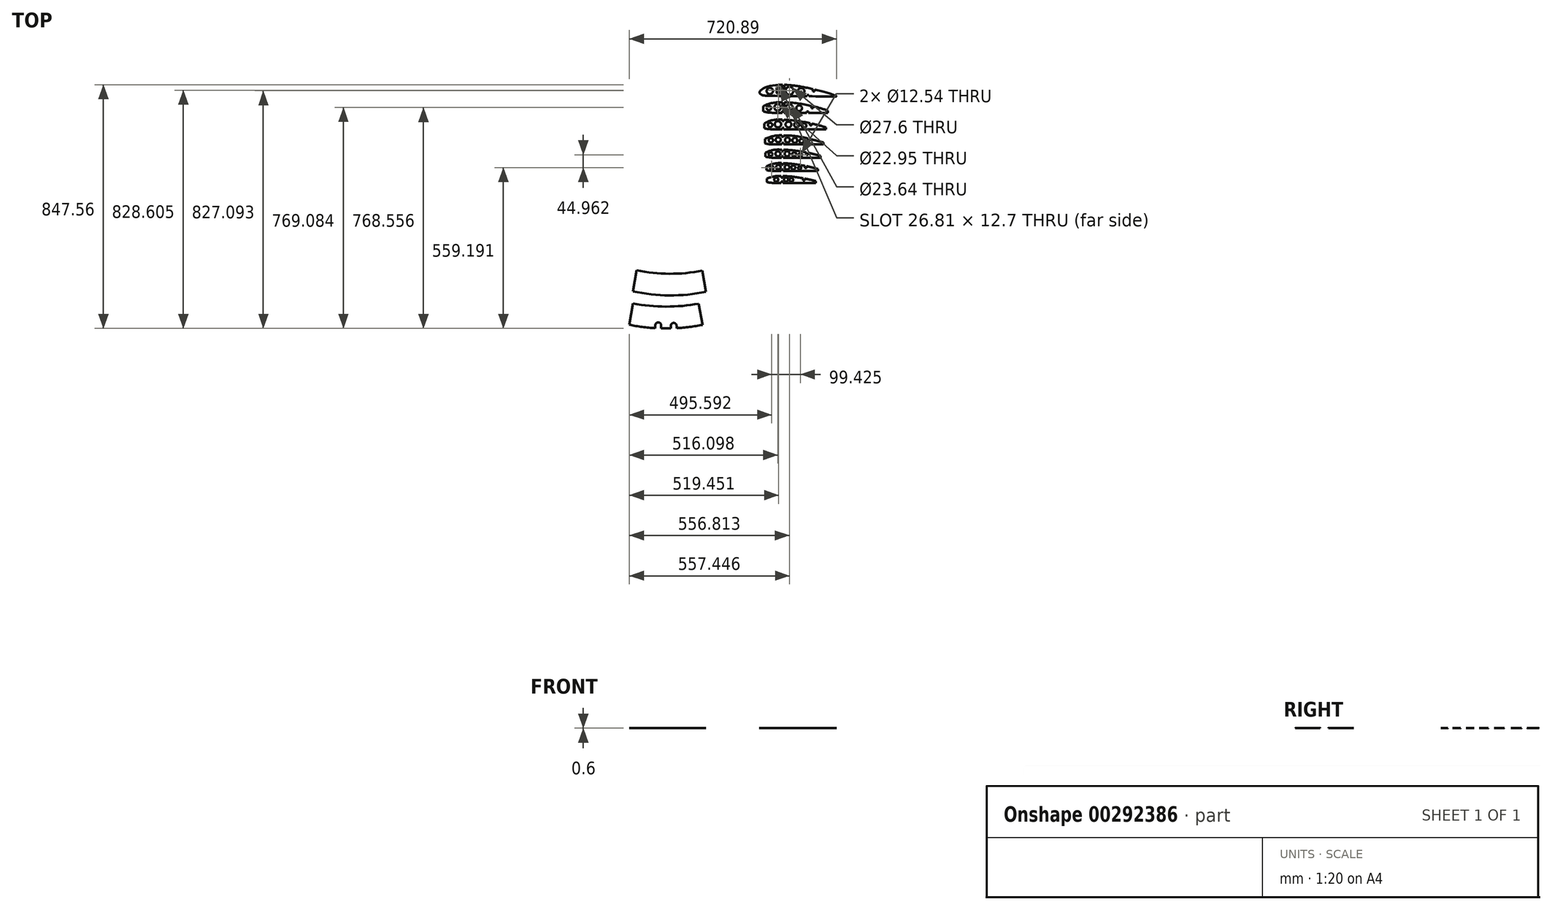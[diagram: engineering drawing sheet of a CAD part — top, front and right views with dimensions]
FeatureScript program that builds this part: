
annotation { "Feature Type Name" : "Feature", "Feature Type Description" : "" }
export const myFeature = defineFeature(function(context is Context, id is Id, definition is map)
    precondition{}
    {
        {
            var Q0;
            Q0=qCreatedBy(makeId("Top.planeOp"),FACE);
            var sketch = newSketch(context, id + "F0", { "sketchPlane" : qUnion([Q0])});
            skLineSegment(sketch, "E0", {"start": v(-635.43, 66.37) * mm, "end": v(-635.43, -80.7) * mm, "construction": true});
            skLineSegment(sketch, "E1", {"start": v(583.77, 66.37) * mm, "end": v(583.77, -80.7) * mm});
            skFitSpline(sketch, "E2", {"points": [v(1167.92, 673) * mm, v(1212.27, 687.2) * mm, v(1331.91, 676.7) * mm, v(1427.16, 648.54) * mm, v(1406.4, 647.5) * mm, v(1225.72, 649.7) * mm, v(1185.23, 650.62) * mm, v(1169.62, 652.52) * mm, v(1159.15, 659.86) * mm, v(1167.92, 673) * mm]});
            skCircle(sketch, "E3", {"center": v(1195.44, 667.12) * mm, "radius": 11.06 * mm});
            skPoint(sketch, "E3.first.point", {"position": v(1192.6, 677.8) * mm});
            skPoint(sketch, "E3.second.point", {"position": v(1197.2, 656.2) * mm});
            skPoint(sketch, "E3.third.point", {"position": v(1206.4, 668.61) * mm});
            skCircle(sketch, "E4", {"center": v(1263.88, 667.96) * mm, "radius": 13.8 * mm});
            skPoint(sketch, "E4.first.point", {"position": v(1256.53, 679.65) * mm});
            skPoint(sketch, "E4.second.point", {"position": v(1261.02, 654.46) * mm});
            skPoint(sketch, "E4.third.point", {"position": v(1275.72, 675.05) * mm});
            skCircle(sketch, "E5", {"center": v(1304.3, 666.16) * mm, "radius": 11.36 * mm});
            skPoint(sketch, "E5.first.point", {"position": v(1295.16, 659.41) * mm});
            skPoint(sketch, "E5.second.point", {"position": v(1313.1, 658.95) * mm});
            skPoint(sketch, "E5.third.point", {"position": v(1311.38, 675.05) * mm});
            skLineSegment(sketch, "E6.bottom", {"start": v(1239.93, 688.41) * mm, "end": v(1246.28, 688.41) * mm});
            skLineSegment(sketch, "E6.top", {"start": v(1239.93, 674.23) * mm, "end": v(1246.28, 674.23) * mm});
            skLineSegment(sketch, "E6.left", {"start": v(1239.93, 688.41) * mm, "end": v(1239.93, 674.23) * mm});
            skLineSegment(sketch, "E6.right", {"start": v(1246.28, 688.41) * mm, "end": v(1246.28, 674.23) * mm});
            skLineSegment(sketch, "E7.bottom", {"start": v(1239.93, 655.28) * mm, "end": v(1246.28, 655.28) * mm});
            skLineSegment(sketch, "E7.top", {"start": v(1239.93, 649.45) * mm, "end": v(1246.28, 649.45) * mm});
            skLineSegment(sketch, "E7.left", {"start": v(1239.93, 655.28) * mm, "end": v(1239.93, 649.45) * mm});
            skLineSegment(sketch, "E7.right", {"start": v(1246.28, 655.28) * mm, "end": v(1246.28, 649.45) * mm});
            skLineSegment(sketch, "E8.bottom", {"start": v(1324.2, 653.14) * mm, "end": v(1330.54, 653.14) * mm});
            skLineSegment(sketch, "E8.top", {"start": v(1324.2, 648.64) * mm, "end": v(1330.54, 648.64) * mm});
            skLineSegment(sketch, "E8.left", {"start": v(1324.2, 653.14) * mm, "end": v(1324.2, 648.64) * mm});
            skLineSegment(sketch, "E8.right", {"start": v(1330.54, 653.14) * mm, "end": v(1330.54, 648.64) * mm});
            skLineSegment(sketch, "E9.bottom", {"start": v(1345.1, 673.75) * mm, "end": v(1351.44, 673.75) * mm});
            skLineSegment(sketch, "E9.top", {"start": v(1345.1, 665.75) * mm, "end": v(1351.44, 665.75) * mm});
            skLineSegment(sketch, "E9.left", {"start": v(1345.1, 673.75) * mm, "end": v(1345.1, 665.75) * mm});
            skLineSegment(sketch, "E9.right", {"start": v(1351.44, 673.75) * mm, "end": v(1351.44, 665.75) * mm});
            skLineSegment(sketch, "E10.bottom", {"start": v(1225.88, 682.88) * mm, "end": v(1225.88, 682.88) * mm});
            skLineSegment(sketch, "E10.top", {"start": v(1225.88, 656.07) * mm, "end": v(1225.88, 656.07) * mm});
            skLineSegment(sketch, "E10.left", {"start": v(1219.53, 676.53) * mm, "end": v(1219.53, 662.42) * mm});
            skLineSegment(sketch, "E10.right", {"start": v(1232.23, 676.53) * mm, "end": v(1232.23, 662.42) * mm});
            skPoint(sketch, "E11.visualSharp", {"position": v(1219.53, 682.88) * mm});
            skArc(sketch, "E11.filletArc", {"start": v(1225.88, 682.88) * mm, "mid": v(1221.4, 681.02) * mm, "end": v(1219.53, 676.53) * mm});
            skPoint(sketch, "E12.visualSharp", {"position": v(1232.23, 682.88) * mm});
            skArc(sketch, "E12.filletArc", {"start": v(1232.23, 676.53) * mm, "mid": v(1230.37, 681.02) * mm, "end": v(1225.88, 682.88) * mm});
            skPoint(sketch, "E13.visualSharp", {"position": v(1232.23, 656.07) * mm});
            skArc(sketch, "E13.filletArc", {"start": v(1225.88, 656.07) * mm, "mid": v(1230.37, 657.93) * mm, "end": v(1232.23, 662.42) * mm});
            skPoint(sketch, "E14.visualSharp", {"position": v(1219.53, 656.07) * mm});
            skArc(sketch, "E14.filletArc", {"start": v(1219.53, 662.42) * mm, "mid": v(1221.4, 657.93) * mm, "end": v(1225.88, 656.07) * mm});
            skLineSegment(sketch, "E15", {"start": v(1172.44, 614.01) * mm, "end": v(1172.44, 595.84) * mm});
            skCircle(sketch, "E16", {"center": v(1192.19, 607.89) * mm, "radius": 7.81 * mm});
            skPoint(sketch, "E16.first.point", {"position": v(1190.06, 615.4) * mm});
            skPoint(sketch, "E16.second.point", {"position": v(1187.28, 601.8) * mm});
            skPoint(sketch, "E16.third.point", {"position": v(1199.5, 605.13) * mm});
            skCircle(sketch, "E17", {"center": v(1222.53, 609.95) * mm, "radius": 11.48 * mm});
            skPoint(sketch, "E17.first.point", {"position": v(1216.7, 619.84) * mm});
            skPoint(sketch, "E17.second.point", {"position": v(1213.92, 602.36) * mm});
            skPoint(sketch, "E17.third.point", {"position": v(1232.52, 604.3) * mm});
            skCircle(sketch, "E18", {"center": v(1263.24, 609.43) * mm, "radius": 11.82 * mm});
            skPoint(sketch, "E18.first.point", {"position": v(1251.66, 611.8) * mm});
            skPoint(sketch, "E18.second.point", {"position": v(1270.53, 618.73) * mm});
            skPoint(sketch, "E18.third.point", {"position": v(1268.87, 599.03) * mm});
            skCircle(sketch, "E19", {"center": v(1297.2, 606.9) * mm, "radius": 9.83 * mm});
            skPoint(sketch, "E19.first.point", {"position": v(1288.85, 612.07) * mm});
            skPoint(sketch, "E19.second.point", {"position": v(1303, 614.85) * mm});
            skPoint(sketch, "E19.third.point", {"position": v(1296.62, 597.09) * mm});
            skLineSegment(sketch, "E20", {"start": v(1397.44, 598.52) * mm, "end": v(1397.44, 590.73) * mm});
            skLineSegment(sketch, "E21", {"start": v(1397.44, 590.73) * mm, "end": v(1245.2, 590.73) * mm});
            skArc(sketch, "E22", {"start": v(1172.44, 595.84) * mm, "mid": v(1188.84, 592.55) * mm, "end": v(1205.5, 591.12) * mm});
            skLineSegment(sketch, "E23", {"start": v(1205.5, 591.12) * mm, "end": v(1238.86, 590.79) * mm});
            skLineSegment(sketch, "E24", {"start": v(1239.93, 649.45) * mm, "end": v(1232.52, 244.45) * mm, "construction": true});
            skLineSegment(sketch, "E25", {"start": v(1246.28, 649.45) * mm, "end": v(1244.15, 533.35) * mm, "construction": true});
            skArc(sketch, "E26", {"start": v(1239.53, 627.83) * mm, "mid": v(1205.1, 625.27) * mm, "end": v(1172.44, 614.01) * mm});
            skLineSegment(sketch, "E27", {"start": v(1239.53, 627.83) * mm, "end": v(1239.28, 613.71) * mm});
            skLineSegment(sketch, "E28", {"start": v(1239.28, 613.71) * mm, "end": v(1245.62, 613.6) * mm});
            skLineSegment(sketch, "E29", {"start": v(1245.62, 613.6) * mm, "end": v(1245.62, 627.83) * mm});
            skLineSegment(sketch, "E30", {"start": v(1238.86, 590.79) * mm, "end": v(1238.98, 597.55) * mm});
            skLineSegment(sketch, "E31", {"start": v(1238.98, 597.55) * mm, "end": v(1245.33, 597.44) * mm});
            skLineSegment(sketch, "E32", {"start": v(1245.33, 597.44) * mm, "end": v(1245.2, 590.73) * mm});
            skArc(sketch, "E33", {"start": v(1397.44, 598.52) * mm, "mid": v(1322.63, 618.85) * mm, "end": v(1245.62, 627.83) * mm});
            skLineSegment(sketch, "E34.bottom", {"start": v(1324.04, 590.73) * mm, "end": v(1330.39, 590.73) * mm});
            skLineSegment(sketch, "E34.top", {"start": v(1324.04, 595.23) * mm, "end": v(1330.39, 595.23) * mm});
            skLineSegment(sketch, "E34.left", {"start": v(1324.04, 590.73) * mm, "end": v(1324.04, 595.23) * mm});
            skLineSegment(sketch, "E34.right", {"start": v(1330.39, 590.73) * mm, "end": v(1330.39, 595.23) * mm});
            skLineSegment(sketch, "E35.bottom", {"start": v(1339.96, 615.2) * mm, "end": v(1346.3, 615.2) * mm});
            skLineSegment(sketch, "E35.top", {"start": v(1339.96, 607.2) * mm, "end": v(1346.3, 607.2) * mm});
            skLineSegment(sketch, "E35.left", {"start": v(1339.96, 615.2) * mm, "end": v(1339.96, 607.2) * mm});
            skLineSegment(sketch, "E35.right", {"start": v(1346.3, 615.2) * mm, "end": v(1346.3, 607.2) * mm});
            skLineSegment(sketch, "E36", {"start": v(1175.58, 553.67) * mm, "end": v(1175.58, 537.08) * mm});
            skLineSegment(sketch, "E37", {"start": v(1238.43, 567.5) * mm, "end": v(1238.35, 563.2) * mm});
            skLineSegment(sketch, "E38", {"start": v(1238.35, 563.2) * mm, "end": v(1244.7, 563.08) * mm});
            skLineSegment(sketch, "E39", {"start": v(1244.7, 563.08) * mm, "end": v(1244.78, 567.34) * mm});
            skArc(sketch, "E40", {"start": v(1238.43, 567.5) * mm, "mid": v(1205.9, 565.58) * mm, "end": v(1175.58, 553.67) * mm});
            skLineSegment(sketch, "E41", {"start": v(1237.8, 533.35) * mm, "end": v(1237.9, 538.62) * mm});
            skLineSegment(sketch, "E42", {"start": v(1237.9, 538.62) * mm, "end": v(1244.25, 538.5) * mm});
            skLineSegment(sketch, "E43", {"start": v(1244.25, 538.5) * mm, "end": v(1244.15, 533.35) * mm});
            skLineSegment(sketch, "E44", {"start": v(1244.15, 533.35) * mm, "end": v(1391.1, 533.35) * mm});
            skLineSegment(sketch, "E45", {"start": v(1391.1, 533.35) * mm, "end": v(1391.1, 539.96) * mm});
            skArc(sketch, "E46", {"start": v(1391.1, 539.96) * mm, "mid": v(1318.8, 558.31) * mm, "end": v(1244.78, 567.34) * mm});
            skLineSegment(sketch, "E47", {"start": v(1237.8, 533.35) * mm, "end": v(1201.86, 534.01) * mm});
            skArc(sketch, "E48", {"start": v(1175.58, 537.08) * mm, "mid": v(1188.64, 534.9) * mm, "end": v(1201.86, 534.01) * mm});
            skLineSegment(sketch, "E49.trimOffspring", {"start": v(1244.1, 529.84) * mm, "end": v(1238.87, 244.45) * mm, "construction": true});
            skCircle(sketch, "E50", {"center": v(1196.54, 548.9) * mm, "radius": 7.53 * mm});
            skPoint(sketch, "E50.first.point", {"position": v(1190.05, 552.74) * mm});
            skPoint(sketch, "E50.second.point", {"position": v(1203.63, 551.45) * mm});
            skPoint(sketch, "E50.third.point", {"position": v(1194.67, 541.6) * mm});
            skCircle(sketch, "E51", {"center": v(1223.69, 551.25) * mm, "radius": 10.95 * mm});
            skPoint(sketch, "E51.first.point", {"position": v(1213.48, 555.21) * mm});
            skPoint(sketch, "E51.second.point", {"position": v(1233.9, 555.21) * mm});
            skPoint(sketch, "E51.third.point", {"position": v(1222.61, 540.35) * mm});
            skCircle(sketch, "E52", {"center": v(1260.28, 550.39) * mm, "radius": 10.09 * mm});
            skPoint(sketch, "E52.first.point", {"position": v(1251.63, 555.57) * mm});
            skPoint(sketch, "E52.second.point", {"position": v(1269.72, 553.96) * mm});
            skPoint(sketch, "E52.third.point", {"position": v(1259.33, 540.35) * mm});
            skCircle(sketch, "E53", {"center": v(1288.67, 549.27) * mm, "radius": 8.94 * mm});
            skPoint(sketch, "E53.first.point", {"position": v(1281.54, 554.68) * mm});
            skPoint(sketch, "E53.second.point", {"position": v(1297.12, 552.17) * mm});
            skPoint(sketch, "E53.third.point", {"position": v(1288.17, 540.35) * mm});
            skCircle(sketch, "E54", {"center": v(1314.2, 546.41) * mm, "radius": 8.16 * mm});
            skPoint(sketch, "E54.first.point", {"position": v(1307.51, 551.1) * mm});
            skPoint(sketch, "E54.second.point", {"position": v(1321.13, 550.74) * mm});
            skPoint(sketch, "E54.third.point", {"position": v(1312.17, 538.5) * mm});
            skLineSegment(sketch, "E55.bottom", {"start": v(1335.4, 554.96) * mm, "end": v(1341.75, 554.96) * mm});
            skLineSegment(sketch, "E55.top", {"start": v(1335.4, 546.96) * mm, "end": v(1341.75, 546.96) * mm});
            skLineSegment(sketch, "E55.left", {"start": v(1335.4, 554.96) * mm, "end": v(1335.4, 546.96) * mm});
            skLineSegment(sketch, "E55.right", {"start": v(1341.75, 554.96) * mm, "end": v(1341.75, 546.96) * mm});
            skLineSegment(sketch, "E56", {"start": v(1178.22, 500.08) * mm, "end": v(1178.22, 484.8) * mm});
            skLineSegment(sketch, "E57", {"start": v(1180.42, 452.56) * mm, "end": v(1180.42, 438.63) * mm});
            skLineSegment(sketch, "E58", {"start": v(1237.43, 512.6) * mm, "end": v(1237.33, 507.52) * mm});
            skLineSegment(sketch, "E59", {"start": v(1237.33, 507.52) * mm, "end": v(1243.68, 507.4) * mm});
            skLineSegment(sketch, "E60", {"start": v(1243.68, 507.4) * mm, "end": v(1243.77, 512.32) * mm});
            skArc(sketch, "E61", {"start": v(1237.43, 512.6) * mm, "mid": v(1207.05, 509.97) * mm, "end": v(1178.22, 500.08) * mm});
            skCircle(sketch, "E62", {"center": v(1199.28, 495.3) * mm, "radius": 7.43 * mm});
            skPoint(sketch, "E62.first.point", {"position": v(1192.54, 498.42) * mm});
            skPoint(sketch, "E62.second.point", {"position": v(1205.96, 498.55) * mm});
            skPoint(sketch, "E62.third.point", {"position": v(1199.88, 487.9) * mm});
            skCircle(sketch, "E63", {"center": v(1224.45, 497.03) * mm, "radius": 8.67 * mm});
            skPoint(sketch, "E63.first.point", {"position": v(1217.24, 501.84) * mm});
            skPoint(sketch, "E63.second.point", {"position": v(1232.18, 500.95) * mm});
            skPoint(sketch, "E63.third.point", {"position": v(1226.23, 488.54) * mm});
            skCircle(sketch, "E64", {"center": v(1256.82, 496.53) * mm, "radius": 8.8 * mm});
            skPoint(sketch, "E64.first.point", {"position": v(1250.28, 502.4) * mm});
            skPoint(sketch, "E64.second.point", {"position": v(1265.5, 498.01) * mm});
            skPoint(sketch, "E64.third.point", {"position": v(1254, 488.2) * mm});
            skCircle(sketch, "E65", {"center": v(1282.36, 495.23) * mm, "radius": 8.73 * mm});
            skPoint(sketch, "E65.first.point", {"position": v(1275.3, 500.38) * mm});
            skPoint(sketch, "E65.second.point", {"position": v(1290.51, 498.35) * mm});
            skPoint(sketch, "E65.third.point", {"position": v(1282.9, 486.51) * mm});
            skCircle(sketch, "E66", {"center": v(1305.97, 493.08) * mm, "radius": 7.41 * mm});
            skPoint(sketch, "E66.first.point", {"position": v(1300.15, 497.67) * mm});
            skPoint(sketch, "E66.second.point", {"position": v(1313.34, 492.26) * mm});
            skPoint(sketch, "E66.third.point", {"position": v(1305.73, 485.67) * mm});
            skLineSegment(sketch, "E67", {"start": v(1243.2, 480.93) * mm, "end": v(1381.45, 480.93) * mm});
            skLineSegment(sketch, "E68", {"start": v(1381.45, 480.93) * mm, "end": v(1381.45, 487.7) * mm});
            skArc(sketch, "E69", {"start": v(1381.45, 487.7) * mm, "mid": v(1355.5, 494.9) * mm, "end": v(1329.23, 500.8) * mm});
            skArc(sketch, "E70", {"start": v(1329.23, 500.8) * mm, "mid": v(1286.9, 509.58) * mm, "end": v(1243.77, 512.32) * mm});
            skLineSegment(sketch, "E71.bottom", {"start": v(1328.35, 501.04) * mm, "end": v(1334.7, 501.04) * mm});
            skLineSegment(sketch, "E71.top", {"start": v(1328.35, 493.04) * mm, "end": v(1334.7, 493.04) * mm});
            skLineSegment(sketch, "E71.left", {"start": v(1328.35, 501.04) * mm, "end": v(1328.35, 493.04) * mm});
            skLineSegment(sketch, "E71.right", {"start": v(1334.7, 501.04) * mm, "end": v(1334.7, 493.04) * mm});
            skLineSegment(sketch, "E72", {"start": v(1236.85, 480.93) * mm, "end": v(1205.6, 480.93) * mm});
            skArc(sketch, "E73", {"start": v(1178.22, 484.8) * mm, "mid": v(1191.78, 481.9) * mm, "end": v(1205.6, 480.93) * mm});
            skLineSegment(sketch, "E74", {"start": v(1236.85, 480.93) * mm, "end": v(1236.94, 486.3) * mm});
            skLineSegment(sketch, "E75", {"start": v(1236.94, 486.3) * mm, "end": v(1243.3, 486.19) * mm});
            skLineSegment(sketch, "E76", {"start": v(1243.3, 486.19) * mm, "end": v(1243.2, 480.93) * mm});
            skLineSegment(sketch, "E77", {"start": v(1216.24, 434.39) * mm, "end": v(1236, 434.39) * mm});
            skLineSegment(sketch, "E78", {"start": v(1371.2, 434.39) * mm, "end": v(1371.33, 440.94) * mm});
            skArc(sketch, "E79", {"start": v(1180.42, 438.63) * mm, "mid": v(1198.2, 435.45) * mm, "end": v(1216.24, 434.39) * mm});
            skLineSegment(sketch, "E80", {"start": v(1226.45, 463.1) * mm, "end": v(1236.52, 462.91) * mm});
            skArc(sketch, "E81", {"start": v(1226.45, 463.1) * mm, "mid": v(1202.8, 460.64) * mm, "end": v(1180.42, 452.56) * mm});
            skLineSegment(sketch, "E82", {"start": v(1236.52, 462.91) * mm, "end": v(1236.42, 457.67) * mm});
            skLineSegment(sketch, "E83", {"start": v(1236.42, 457.67) * mm, "end": v(1242.77, 457.56) * mm});
            skLineSegment(sketch, "E84", {"start": v(1242.77, 457.56) * mm, "end": v(1242.86, 462.8) * mm});
            skArc(sketch, "E85", {"start": v(1371.33, 440.94) * mm, "mid": v(1307.79, 455.94) * mm, "end": v(1242.86, 462.8) * mm});
            skCircle(sketch, "E86", {"center": v(1198.04, 447.16) * mm, "radius": 6.7 * mm});
            skPoint(sketch, "E86.first.point", {"position": v(1192.54, 450.98) * mm});
            skPoint(sketch, "E86.second.point", {"position": v(1204.49, 449) * mm});
            skPoint(sketch, "E86.third.point", {"position": v(1197.95, 440.46) * mm});
            skCircle(sketch, "E87", {"center": v(1223.52, 448.32) * mm, "radius": 8.72 * mm});
            skPoint(sketch, "E87.first.point", {"position": v(1216.14, 452.97) * mm});
            skPoint(sketch, "E87.second.point", {"position": v(1231.5, 451.83) * mm});
            skPoint(sketch, "E87.third.point", {"position": v(1223.25, 439.6) * mm});
            skCircle(sketch, "E88", {"center": v(1255.6, 448.56) * mm, "radius": 8.67 * mm});
            skPoint(sketch, "E88.first.point", {"position": v(1247.99, 452.69) * mm});
            skPoint(sketch, "E88.second.point", {"position": v(1263.63, 451.83) * mm});
            skPoint(sketch, "E88.third.point", {"position": v(1255.38, 439.9) * mm});
            skCircle(sketch, "E89", {"center": v(1280, 446.72) * mm, "radius": 7.4 * mm});
            skPoint(sketch, "E89.first.point", {"position": v(1273.58, 450.41) * mm});
            skPoint(sketch, "E89.second.point", {"position": v(1286.94, 449.28) * mm});
            skPoint(sketch, "E89.third.point", {"position": v(1279.83, 439.32) * mm});
            skCircle(sketch, "E90", {"center": v(1301.45, 445.02) * mm, "radius": 6.27 * mm});
            skPoint(sketch, "E90.first.point", {"position": v(1302.01, 451.27) * mm});
            skPoint(sketch, "E90.second.point", {"position": v(1305.42, 440.18) * mm});
            skPoint(sketch, "E90.third.point", {"position": v(1301.44, 438.76) * mm});
            skLineSegment(sketch, "E91.bottom", {"start": v(1322.8, 453.16) * mm, "end": v(1329.15, 453.16) * mm});
            skLineSegment(sketch, "E91.top", {"start": v(1322.8, 445.16) * mm, "end": v(1329.15, 445.16) * mm});
            skLineSegment(sketch, "E91.left", {"start": v(1322.8, 453.16) * mm, "end": v(1322.8, 445.16) * mm});
            skLineSegment(sketch, "E91.right", {"start": v(1329.15, 453.16) * mm, "end": v(1329.15, 445.16) * mm});
            skLineSegment(sketch, "E92", {"start": v(1236, 434.39) * mm, "end": v(1236.09, 439.66) * mm});
            skLineSegment(sketch, "E93", {"start": v(1236.09, 439.66) * mm, "end": v(1242.44, 439.54) * mm});
            skLineSegment(sketch, "E94", {"start": v(1242.44, 439.54) * mm, "end": v(1242.44, 434.39) * mm});
            skLineSegment(sketch, "E95.trimOffspring", {"start": v(1242.34, 434.39) * mm, "end": v(1371.2, 434.39) * mm});
            skLineSegment(sketch, "E96", {"start": v(1184.02, 405.49) * mm, "end": v(1184.02, 391.26) * mm});
            skLineSegment(sketch, "E97", {"start": v(1363.3, 395.02) * mm, "end": v(1363.3, 388.58) * mm});
            skLineSegment(sketch, "E98", {"start": v(1363.3, 388.58) * mm, "end": v(1241.5, 388.58) * mm});
            skLineSegment(sketch, "E99", {"start": v(1235.15, 388.58) * mm, "end": v(1235.25, 393.94) * mm});
            skLineSegment(sketch, "E100", {"start": v(1235.25, 393.94) * mm, "end": v(1241.6, 393.83) * mm});
            skLineSegment(sketch, "E101", {"start": v(1241.6, 393.83) * mm, "end": v(1241.6, 388.58) * mm});
            skLineSegment(sketch, "E102", {"start": v(1235.66, 416.17) * mm, "end": v(1235.56, 410.6) * mm});
            skLineSegment(sketch, "E103", {"start": v(1235.56, 410.6) * mm, "end": v(1241.9, 410.47) * mm});
            skLineSegment(sketch, "E104", {"start": v(1241.9, 410.47) * mm, "end": v(1242, 416.04) * mm});
            skArc(sketch, "E105", {"start": v(1363.3, 395.02) * mm, "mid": v(1303.27, 409.1) * mm, "end": v(1242, 416.04) * mm});
            skArc(sketch, "E106", {"start": v(1235.66, 416.17) * mm, "mid": v(1209.16, 414.1) * mm, "end": v(1184.02, 405.49) * mm});
            skArc(sketch, "E107", {"start": v(1184.02, 391.26) * mm, "mid": v(1200.74, 389.25) * mm, "end": v(1217.57, 388.58) * mm});
            skCircle(sketch, "E108", {"center": v(1224.9, 401.89) * mm, "radius": 7.9 * mm});
            skPoint(sketch, "E108.first.point", {"position": v(1218.16, 406) * mm});
            skPoint(sketch, "E108.second.point", {"position": v(1232.38, 404.42) * mm});
            skPoint(sketch, "E108.third.point", {"position": v(1224.03, 394.04) * mm});
            skCircle(sketch, "E109", {"center": v(1202.02, 400.06) * mm, "radius": 6.27 * mm});
            skPoint(sketch, "E109.first.point", {"position": v(1196.95, 403.74) * mm});
            skPoint(sketch, "E109.second.point", {"position": v(1208, 401.94) * mm});
            skPoint(sketch, "E109.third.point", {"position": v(1201.46, 393.82) * mm});
            skCircle(sketch, "E110", {"center": v(1255.17, 401.6) * mm, "radius": 8.26 * mm});
            skPoint(sketch, "E110.first.point", {"position": v(1248.85, 406.9) * mm});
            skPoint(sketch, "E110.second.point", {"position": v(1262.84, 404.65) * mm});
            skPoint(sketch, "E110.third.point", {"position": v(1257.2, 393.59) * mm});
            skCircle(sketch, "E111", {"center": v(1276.97, 401.16) * mm, "radius": 7.2 * mm});
            skPoint(sketch, "E111.first.point", {"position": v(1271.87, 406.23) * mm});
            skPoint(sketch, "E111.second.point", {"position": v(1283.38, 404.42) * mm});
            skPoint(sketch, "E111.third.point", {"position": v(1275.93, 394.04) * mm});
            skCircle(sketch, "E112", {"center": v(1298.97, 399.13) * mm, "radius": 5.4 * mm});
            skPoint(sketch, "E112.first.point", {"position": v(1294.66, 402.4) * mm});
            skPoint(sketch, "E112.second.point", {"position": v(1304.37, 399) * mm});
            skPoint(sketch, "E112.third.point", {"position": v(1298.05, 393.82) * mm});
            skLineSegment(sketch, "E113.trimOffspring", {"start": v(1235.15, 388.58) * mm, "end": v(1217.57, 388.58) * mm});
            skLineSegment(sketch, "E114.bottom", {"start": v(1317.14, 406.5) * mm, "end": v(1323.5, 406.5) * mm});
            skLineSegment(sketch, "E114.top", {"start": v(1317.14, 398.5) * mm, "end": v(1323.5, 398.5) * mm});
            skLineSegment(sketch, "E114.left", {"start": v(1317.14, 406.5) * mm, "end": v(1317.14, 398.5) * mm});
            skLineSegment(sketch, "E114.right", {"start": v(1323.5, 406.5) * mm, "end": v(1323.5, 398.5) * mm});
            skLineSegment(sketch, "E115", {"start": v(1184.93, 361.62) * mm, "end": v(1184.93, 350.17) * mm});
            skLineSegment(sketch, "E116", {"start": v(1354.82, 353.49) * mm, "end": v(1354.82, 347.16) * mm});
            skLineSegment(sketch, "E117", {"start": v(1354.82, 347.16) * mm, "end": v(1240.75, 347.16) * mm});
            skLineSegment(sketch, "E118", {"start": v(1234.4, 347.16) * mm, "end": v(1234.5, 352.36) * mm});
            skLineSegment(sketch, "E119", {"start": v(1234.5, 352.36) * mm, "end": v(1240.84, 352.36) * mm});
            skLineSegment(sketch, "E120", {"start": v(1240.84, 352.36) * mm, "end": v(1240.84, 347.16) * mm});
            skLineSegment(sketch, "E121.trimOffspring", {"start": v(1234.4, 347.16) * mm, "end": v(1208.42, 347.16) * mm});
            skArc(sketch, "E122", {"start": v(1184.93, 350.17) * mm, "mid": v(1196.58, 347.92) * mm, "end": v(1208.42, 347.16) * mm});
            skLineSegment(sketch, "E123", {"start": v(1234.84, 371.36) * mm, "end": v(1234.75, 366.23) * mm});
            skLineSegment(sketch, "E124", {"start": v(1234.75, 366.23) * mm, "end": v(1241.1, 366.12) * mm});
            skLineSegment(sketch, "E125", {"start": v(1241.1, 366.12) * mm, "end": v(1241.19, 371.35) * mm});
            skArc(sketch, "E126", {"start": v(1354.82, 353.49) * mm, "mid": v(1298.5, 365.53) * mm, "end": v(1241.19, 371.35) * mm});
            skArc(sketch, "E127", {"start": v(1234.84, 371.36) * mm, "mid": v(1209.27, 369.65) * mm, "end": v(1184.93, 361.62) * mm});
            skCircle(sketch, "E128", {"center": v(1217.84, 358.54) * mm, "radius": 7.11 * mm});
            skPoint(sketch, "E128.first.point", {"position": v(1212.02, 362.62) * mm});
            skPoint(sketch, "E128.second.point", {"position": v(1224.54, 360.92) * mm});
            skPoint(sketch, "E128.third.point", {"position": v(1217.9, 351.43) * mm});
            skCircle(sketch, "E129", {"center": v(1251.8, 359.34) * mm, "radius": 7.14 * mm});
            skPoint(sketch, "E129.first.point", {"position": v(1246.36, 363.95) * mm});
            skPoint(sketch, "E129.second.point", {"position": v(1258.32, 362.24) * mm});
            skPoint(sketch, "E129.third.point", {"position": v(1253.38, 352.38) * mm});
            skCircle(sketch, "E130", {"center": v(1270.34, 357.75) * mm, "radius": 6.34 * mm});
            skPoint(sketch, "E130.first.point", {"position": v(1265.53, 361.87) * mm});
            skPoint(sketch, "E130.second.point", {"position": v(1276.35, 359.78) * mm});
            skPoint(sketch, "E130.third.point", {"position": v(1270.84, 351.43) * mm});
            skLineSegment(sketch, "E131.bottom", {"start": v(1310.3, 363.54) * mm, "end": v(1316.66, 363.54) * mm});
            skLineSegment(sketch, "E131.top", {"start": v(1310.3, 355.54) * mm, "end": v(1316.66, 355.54) * mm});
            skLineSegment(sketch, "E131.left", {"start": v(1310.3, 363.54) * mm, "end": v(1310.3, 355.54) * mm});
            skLineSegment(sketch, "E131.right", {"start": v(1316.66, 363.54) * mm, "end": v(1316.66, 355.54) * mm});
            skSolve(sketch);
        }
        {
            var Q0;
            Q0=makeQuery(id+"F0.imprint","IMPRINT",FACE,{"disambiguationData":[TD([[makeQuery(id+"F0.imprint","IMPRINT",EDGE,{"derivedFrom":sQuery(id+"F0.wireOp",EDGE,"E3")}),-1.0]])]});
            var Q1;
            Q1=makeQuery(id+"F0.imprint","IMPRINT",FACE,{"disambiguationData":[TD([[makeQuery(id+"F0.imprint","IMPRINT",EDGE,{"derivedFrom":sQuery(id+"F0.wireOp",EDGE,"E15")}),1.0]])]});
            var Q2;
            Q2=makeQuery(id+"F0.imprint","IMPRINT",FACE,{"disambiguationData":[TD([[makeQuery(id+"F0.imprint","IMPRINT",EDGE,{"derivedFrom":sQuery(id+"F0.wireOp",EDGE,"E36")}),1.0]])]});
            var Q3;
            Q3=makeQuery(id+"F0.imprint","IMPRINT",FACE,{"disambiguationData":[TD([[makeQuery(id+"F0.imprint","IMPRINT",EDGE,{"derivedFrom":sQuery(id+"F0.wireOp",EDGE,"E56")}),1.0]])]});
            var Q4;
            Q4=makeQuery(id+"F0.imprint","IMPRINT",FACE,{"disambiguationData":[TD([[makeQuery(id+"F0.imprint","IMPRINT",EDGE,{"derivedFrom":sQuery(id+"F0.wireOp",EDGE,"E57")}),1.0]])]});
            var Q5;
            Q5=makeQuery(id+"F0.imprint","IMPRINT",FACE,{"disambiguationData":[TD([[makeQuery(id+"F0.imprint","IMPRINT",EDGE,{"derivedFrom":sQuery(id+"F0.wireOp",EDGE,"E96")}),1.0]])]});
            var Q6;
            Q6=makeQuery(id+"F0.imprint","IMPRINT",FACE,{"disambiguationData":[TD([[makeQuery(id+"F0.imprint","IMPRINT",EDGE,{"derivedFrom":sQuery(id+"F0.wireOp",EDGE,"E115")}),1.0]])]});
            extrude(context, id + "F1", {"entities" : qUnion([Q0, Q1, Q2, Q3, Q4, Q5, Q6]), "depth" : 1 / 406.4 * mm});
        }
        {
            var Q0;
            Q0=qCreatedBy(makeId("Top.planeOp"),FACE);
            var sketch = newSketch(context, id + "F2", { "sketchPlane" : qUnion([Q0])});
            skLineSegment(sketch, "E132", {"start": v(731.68, 43.8) * mm, "end": v(718.95, -29.93) * mm});
            skLineSegment(sketch, "E133", {"start": v(960.2, 42.03) * mm, "end": v(973.01, -31.7) * mm});
            skArc(sketch, "E134", {"start": v(731.68, 43.8) * mm, "mid": v(845.85, 31.15) * mm, "end": v(960.2, 42.03) * mm});
            skArc(sketch, "E135", {"start": v(718.95, -29.93) * mm, "mid": v(845.89, -44.13) * mm, "end": v(973.01, -31.7) * mm});
            skLineSegment(sketch, "E136", {"start": v(719.26, -72.6) * mm, "end": v(706.43, -146.31) * mm});
            skLineSegment(sketch, "E137", {"start": v(948.13, -72.97) * mm, "end": v(960.97, -146.68) * mm});
            skArc(sketch, "E138", {"start": v(719.26, -72.6) * mm, "mid": v(833.68, -83.17) * mm, "end": v(948.13, -72.97) * mm});
            skArc(sketch, "E139", {"start": v(706.43, -146.31) * mm, "mid": v(751.31, -153.75) * mm, "end": v(796.6, -158.01) * mm});
            skArc(sketch, "E140", {"start": v(817.15, -146.31) * mm, "mid": v(806.1, -138.33) * mm, "end": v(796.6, -148.11) * mm});
            skArc(sketch, "E141", {"start": v(870.8, -149.77) * mm, "mid": v(861.1, -139.9) * mm, "end": v(850.67, -149.03) * mm});
            skLineSegment(sketch, "E142", {"start": v(796.6, -158.01) * mm, "end": v(796.6, -148.11) * mm});
            skLineSegment(sketch, "E143", {"start": v(816.3, -158.87) * mm, "end": v(817.15, -146.31) * mm});
            skLineSegment(sketch, "E144", {"start": v(850.94, -158.92) * mm, "end": v(850.67, -149.03) * mm});
            skLineSegment(sketch, "E145", {"start": v(870.96, -158.1) * mm, "end": v(870.8, -149.77) * mm});
            skArc(sketch, "E146.trimOffspring", {"start": v(816.3, -158.87) * mm, "mid": v(833.62, -159.13) * mm, "end": v(850.94, -158.92) * mm});
            skArc(sketch, "E147.trimOffspring", {"start": v(870.96, -158.1) * mm, "mid": v(916.17, -153.97) * mm, "end": v(960.97, -146.68) * mm});
            skLineSegment(sketch, "E148", {"start": v(731.68, 43.8) * mm, "end": v(960.2, 42.03) * mm, "construction": true});
            skLineSegment(sketch, "E149", {"start": v(718.95, -29.93) * mm, "end": v(973.01, -31.7) * mm, "construction": true});
            skLineSegment(sketch, "E150", {"start": v(845.94, 42.03) * mm, "end": v(845.94, -29.93) * mm, "construction": true});
            skPoint(sketch, "E150.startSnap0", {"position": v(845.94, 42.92) * mm});
            skLineSegment(sketch, "E151", {"start": v(719.26, -72.6) * mm, "end": v(948.13, -72.97) * mm, "construction": true});
            skLineSegment(sketch, "E152", {"start": v(706.43, -146.31) * mm, "end": v(960.97, -146.68) * mm, "construction": true});
            skSolve(sketch);
        }
        {
            var Q0;
            Q0=makeQuery(id+"F2.imprint","IMPRINT",FACE,{"disambiguationData":[TD([[makeQuery(id+"F2.imprint","IMPRINT",EDGE,{"derivedFrom":sQuery(id+"F2.wireOp",EDGE,"E132")}),1.0]])]});
            var Q1;
            Q1=makeQuery(id+"F2.imprint","IMPRINT",FACE,{"disambiguationData":[TD([[makeQuery(id+"F2.imprint","IMPRINT",EDGE,{"derivedFrom":sQuery(id+"F2.wireOp",EDGE,"E136")}),1.0]])]});
            extrude(context, id + "F3", {"entities" : qUnion([Q0, Q1]), "depth" : .6 * mm});
        }
    });
